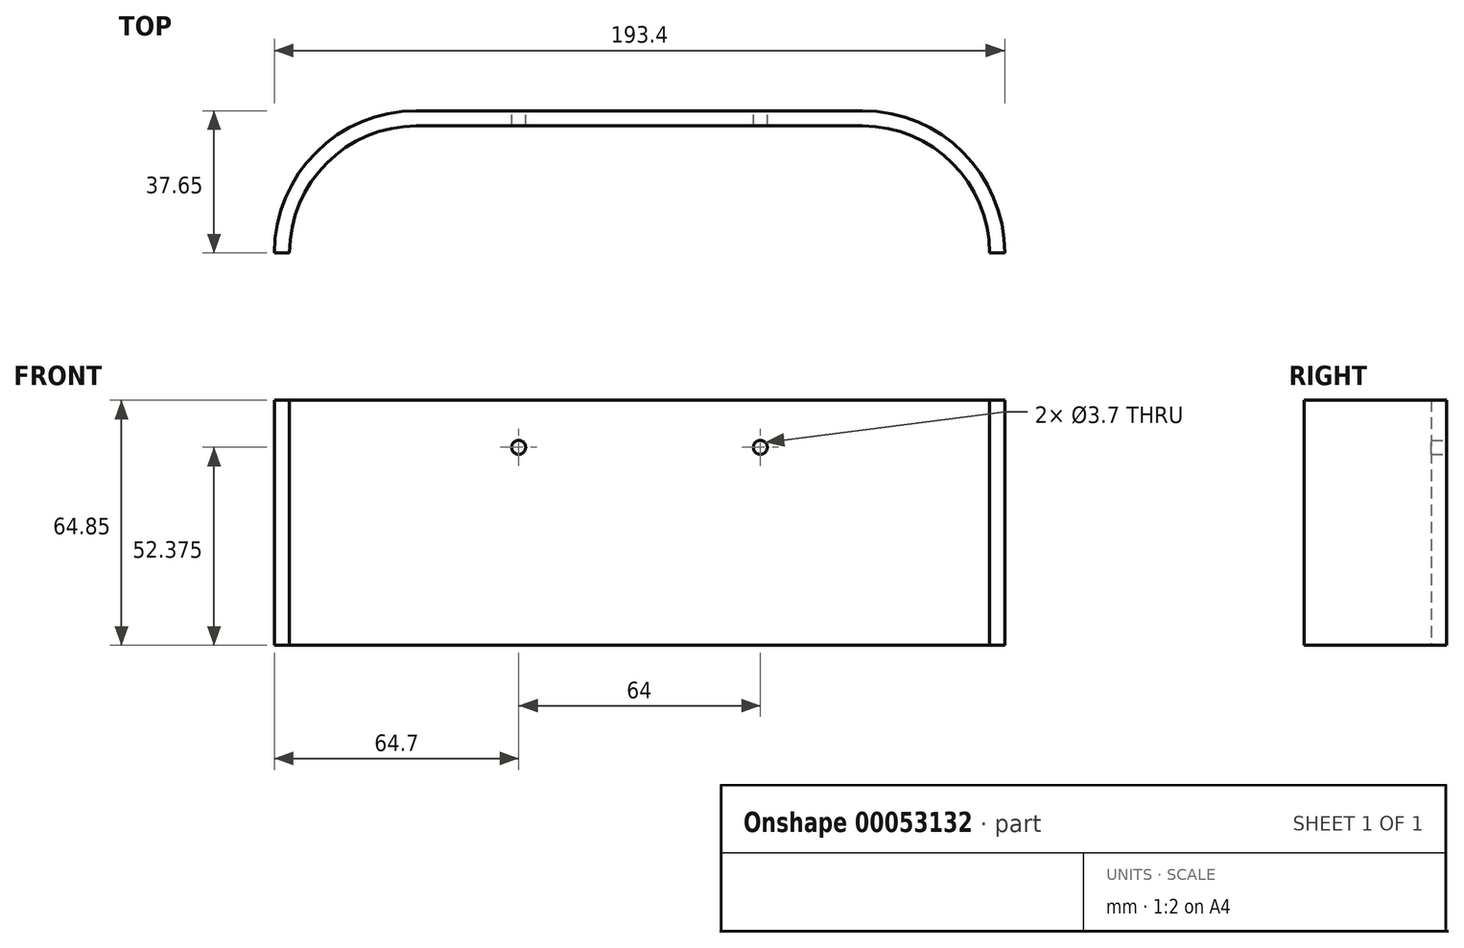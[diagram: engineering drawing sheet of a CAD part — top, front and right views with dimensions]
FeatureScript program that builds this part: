
annotation { "Feature Type Name" : "Feature", "Feature Type Description" : "" }
export const myFeature = defineFeature(function(context is Context, id is Id, definition is map)
    precondition{}
    {
        {
            var Q0;
            Q0=qCreatedBy(makeId("Front.planeOp"),FACE);
            var sketch = newSketch(context, id + "F0", { "sketchPlane" : qUnion([Q0])});
            skLineSegment(sketch, "E0.rect.bottom", {"start": v(59.05, 30.43) * mm, "end": v(-59.05, 30.43) * mm});
            skLineSegment(sketch, "E0.rect.top", {"start": v(59.05, -30.43) * mm, "end": v(-59.05, -30.43) * mm});
            skLineSegment(sketch, "E0.rect.left", {"start": v(59.05, 30.43) * mm, "end": v(59.05, -30.43) * mm});
            skLineSegment(sketch, "E0.rect.right", {"start": v(-59.05, 30.43) * mm, "end": v(-59.05, -30.43) * mm});
            skPoint(sketch, "E0.rect.middle", {"position": v(0, 0) * mm});
            skSolve(sketch);
        }
        {
            var Q0;
            Q0 = qSketchRegion(id + "F0", true);
            extrude(context, id + "F1", {"entities" : qUnion([Q0]), "depth" : 2.5 * mm});
        }
        {
            var Q0;
            {var subQ0=sQuery(id+"F0.wireOp",EDGE,"E0.rect.bottom");Q0=makeQuery(id+"F6.boolean.opBoolean","MERGE",FACE,{"derivedFrom":[makeQuery(id+"F1.opExtrude","CAP_FACE",FACE,{"disambiguationData":[OSD([subQ0,sQuery(id+"F0.wireOp",EDGE,"E0.rect.top"),sQuery(id+"F0.wireOp",EDGE,"E0.rect.left"),sQuery(id+"F0.wireOp",EDGE,"E0.rect.right")])],"isStart":true}),makeQuery(id+"F6.opExtrude","SWEPT_FACE",FACE,{"disambiguationData":[OSD([subQ0]),TDD([makeQuery(id+"F1.opExtrude","CAP_EDGE",EDGE,{"disambiguationData":[OSD([subQ0])],"isStart":true})])]})]});}
            extrude(context, id + "F2", {"entities" : qUnion([Q0]), "operationType" : NewBodyOperationType.ADD, "depth" : 1.5 * mm});
        }
        {
            var Q0;
            Q0=qCreatedBy(makeId("Top.planeOp"),FACE);
            var sketch = newSketch(context, id + "F3", { "sketchPlane" : qUnion([Q0])});
            skPoint(sketch, "E1", {"position": v(59.05, 0) * mm});
            skPoint(sketch, "E2", {"position": v(0, 0) * mm});
            skPoint(sketch, "E3", {"position": v(59.05, -2.5) * mm});
            skPoint(sketch, "E4", {"position": v(-59.05, -2.5) * mm});
            skPoint(sketch, "E5", {"position": v(-59.05, -36.15) * mm});
            skPoint(sketch, "E6", {"position": v(59.05, -36.15) * mm});
            skArc(sketch, "E7", {"start": v(-59.05, -2.5) * mm, "mid": v(-82.84, -12.36) * mm, "end": v(-92.7, -36.15) * mm});
            skArc(sketch, "E8", {"start": v(92.7, -36.15) * mm, "mid": v(82.84, -12.36) * mm, "end": v(59.05, -2.5) * mm});
            skPoint(sketch, "E9", {"position": v(92.7, -36.15) * mm});
            skPoint(sketch, "E10", {"position": v(-92.7, -36.15) * mm});
            skLineSegment(sketch, "E11", {"start": v(-95.2, -36.15) * mm, "end": v(-92.7, -36.15) * mm});
            skLineSegment(sketch, "E12", {"start": v(92.7, -36.15) * mm, "end": v(95.2, -36.15) * mm});
            skLineSegment(sketch, "E13", {"start": v(-59.05, 0) * mm, "end": v(-59.05, -2.5) * mm});
            skLineSegment(sketch, "E14", {"start": v(59.05, 0) * mm, "end": v(59.05, -2.5) * mm});
            skPoint(sketch, "E15", {"position": v(59.05, 1.5) * mm});
            skPoint(sketch, "E16", {"position": v(-59.05, 1.5) * mm});
            skArc(sketch, "E17", {"start": v(-59.05, 1.5) * mm, "mid": v(-85.67, -9.53) * mm, "end": v(-96.7, -36.15) * mm});
            skArc(sketch, "E18", {"start": v(96.7, -36.15) * mm, "mid": v(85.67, -9.53) * mm, "end": v(59.05, 1.5) * mm});
            skPoint(sketch, "E19", {"position": v(96.7, -36.15) * mm});
            skPoint(sketch, "E20", {"position": v(-96.7, -36.15) * mm});
            skLineSegment(sketch, "E21", {"start": v(-92.7, -36.15) * mm, "end": v(-96.7, -36.15) * mm});
            skLineSegment(sketch, "E22", {"start": v(96.7, -36.15) * mm, "end": v(92.7, -36.15) * mm});
            skLineSegment(sketch, "E23", {"start": v(-59.05, 1.5) * mm, "end": v(-59.05, -2.5) * mm});
            skLineSegment(sketch, "E24", {"start": v(59.05, 1.5) * mm, "end": v(59.05, -2.5) * mm});
            skSolve(sketch);
        }
        {
            var Q0;
            Q0 = qSketchRegion(id + "F3", true);
            extrude(context, id + "F4", {"entities" : qUnion([Q0]), "operationType" : NewBodyOperationType.ADD, "depth" : 32.92 * mm});
        }
        {
            var Q0;
            Q0 = qSketchRegion(id + "F3", true);
            extrude(context, id + "F5", {"entities" : qUnion([Q0]), "operationType" : NewBodyOperationType.ADD, "oppositeDirection" : true, "depth" : 30.43 * mm});
        }
        {
            var Q0;
            Q0=makeQuery(id+"F1.opExtrude","SWEPT_FACE",FACE,{"disambiguationData":[OSD([sQuery(id+"F0.wireOp",EDGE,"E0.rect.bottom")])]});
            extrude(context, id + "F6", {"entities" : qUnion([Q0]), "operationType" : NewBodyOperationType.ADD, "depth" : 2.5 * mm});
        }
        {
            var Q0;
            Q0=makeQuery(id+"F6.boolean.opBoolean","MERGE",FACE,{"derivedFrom":[makeQuery(id+"F4.opExtrude","CAP_FACE",FACE,{"disambiguationData":[OSD([sQuery(id+"F3.wireOp",EDGE,"E7"),sQuery(id+"F3.wireOp",EDGE,"E17"),sQuery(id+"F3.wireOp",EDGE,"E21"),sQuery(id+"F3.wireOp",EDGE,"E23")])],"isStart":false}),makeQuery(id+"F4.opExtrude","CAP_FACE",FACE,{"disambiguationData":[OSD([sQuery(id+"F3.wireOp",EDGE,"E8"),sQuery(id+"F3.wireOp",EDGE,"E18"),sQuery(id+"F3.wireOp",EDGE,"E22"),sQuery(id+"F3.wireOp",EDGE,"E24")])],"isStart":false}),makeQuery(id+"F6.opExtrude","CAP_FACE",FACE,{"disambiguationData":[OSD([sQuery(id+"F0.wireOp",EDGE,"E0.rect.bottom")])],"isStart":false})]});
            extrude(context, id + "F7", {"entities" : qUnion([Q0]), "operationType" : NewBodyOperationType.ADD, "depth" : 1.5 * mm});
        }
        {
            var Q0;
            {var subQ0=sQuery(id+"F0.wireOp",EDGE,"E0.rect.bottom");var subQ1=makeQuery(id+"F2.opExtrude","CAP_EDGE",EDGE,{"disambiguationData":[OSD([subQ0])],"isStart":false});Q0=makeQuery(id+"F7.boolean.opBoolean","MERGE",FACE,{"derivedFrom":[makeQuery(id+"F6.boolean.opBoolean","MERGE",FACE,{"derivedFrom":[makeQuery(id+"F2.opExtrude","CAP_FACE",FACE,{"disambiguationData":[OSD([subQ0,sQuery(id+"F0.wireOp",EDGE,"E0.rect.top"),sQuery(id+"F0.wireOp",EDGE,"E0.rect.left"),sQuery(id+"F0.wireOp",EDGE,"E0.rect.right")])],"isStart":false}),makeQuery(id+"F6.opExtrude","SWEPT_FACE",FACE,{"disambiguationData":[OSD([subQ0]),TDD([subQ1])]})]}),makeQuery(id+"F7.opExtrude","SWEPT_FACE",FACE,{"disambiguationData":[OSD([subQ0]),TDD([makeQuery(id+"F6.opExtrude","CAP_EDGE",EDGE,{"disambiguationData":[OSD([subQ0]),TDD([subQ1])],"isStart":false})])]})]});}
            var sketch = newSketch(context, id + "F8", { "sketchPlane" : qUnion([Q0])});
            skLineSegment(sketch, "E25", {"start": v(-32, 21.95) * mm, "end": v(0, 21.95) * mm});
            skCircle(sketch, "E26", {"center": v(-32, 21.95) * mm, "radius": 1.85 * mm});
            skLineSegment(sketch, "E27", {"start": v(0, 21.95) * mm, "end": v(32, 21.95) * mm});
            skCircle(sketch, "E28", {"center": v(32, 21.95) * mm, "radius": 1.85 * mm});
            skLineSegment(sketch, "E29", {"start": v(-32, 23.8) * mm, "end": v(-32, 34.43) * mm});
            skSolve(sketch);
        }
        {
            var Q0;
            Q0 = qSketchRegion(id + "F8", true);
            extrude(context, id + "F9", {"entities" : qUnion([Q0]), "operationType" : NewBodyOperationType.REMOVE, "oppositeDirection" : true, "depth" : 25 * mm});
        }
    });
